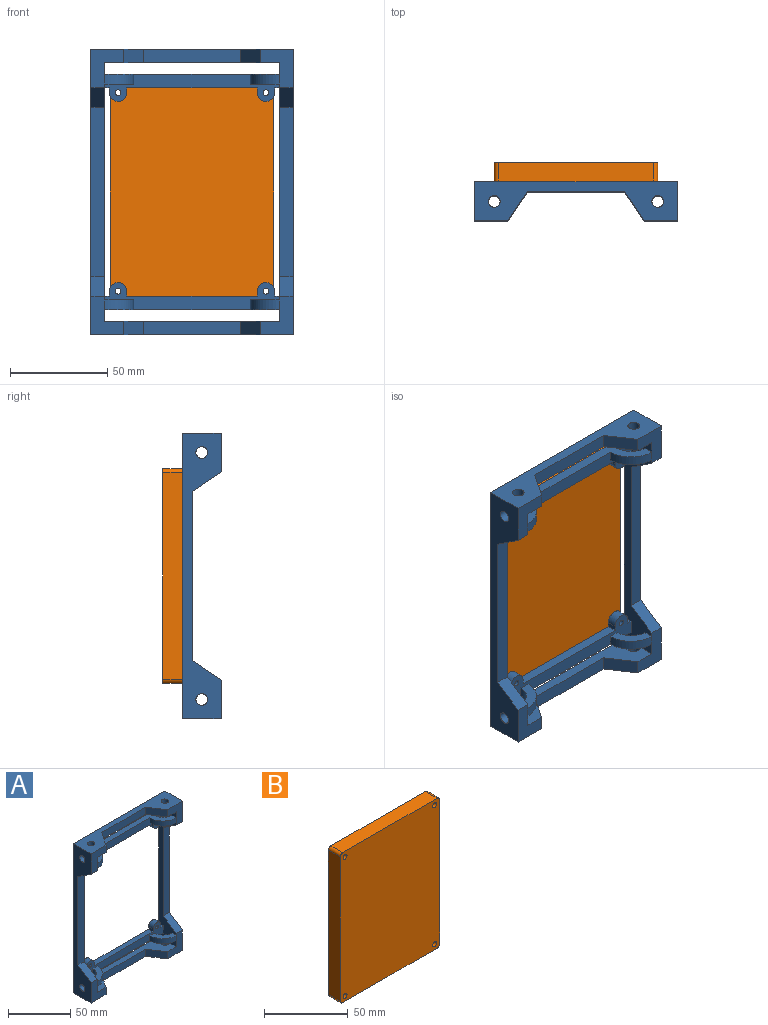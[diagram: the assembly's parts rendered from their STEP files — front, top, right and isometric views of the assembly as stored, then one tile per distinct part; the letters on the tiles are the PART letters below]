
ASSEMBLY  parts=2 mates=1
PART A: 71 faces, bbox 104x20x147 mm
  f0: plane 20x17mm, normal (0,-1,0), area 210mm2, adj f1,f2,f7,f8,f29,f37,f39
  f1: plane 133x20mm, normal (1,0,0), area 1028.5mm2, adj f0,f3,f4,f5,f8,f9,f14,f15
  f2: plane 147x20mm, normal (-1,0,0), area 1428.5mm2, adj f0,f3,f6,f7,f24,f31,f32,f39
  f3: plane 20x17mm, normal (0,-1,0), area 210mm2, adj f1,f2,f6,f21,f25,f33,f40
  f4: plane 90x14mm, normal (0,-1,0), area 674.5mm2, adj f1,f15,f16,f17,f18,f19,f20,f22
  f5: plane 90x14mm, normal (0,-1,0), area 674.5mm2, adj f1,f9,f10,f11,f12,f13,f14,f23
  f6: plane 104x20mm, normal (0,0,1), area 1123.5mm2, adj f2,f3,f24,f33,f34,f35,f44,f45
  f7: plane 104x20mm, normal (0,0,-1), area 1123.5mm2, adj f0,f2,f24,f36,f37,f38,f42,f44
  f8: plane 90x20mm, normal (0,0,1), area 843.5mm2, adj f0,f1,f24,f36,f37,f38,f42,f43
  f9: plane 90x20mm, normal (0,0,-1), area 646.3mm2, adj f1,f5,f24,f28,f29,f43,f59,f60
  f10: plane 67x5mm, normal (0,0,1), area 335mm2, adj f5,f11,f24,f46
  f11: plane 5x2.5mm, normal (1,0,0), area 12.5mm2, adj f5,f10,f12,f24
  f12: cylinder r=4.5mm len=9mm, axis (0,1,0), area 70.7mm2, adj f5,f11,f13,f24
  f13: plane 5x2.5mm, normal (-1,0,0), area 12.5mm2, adj f5,f12,f14,f24
  f14: plane 5x2.5mm, normal (0,0,1), area 12.5mm2, adj f1,f5,f13,f24
  f15: plane 5x2.5mm, normal (0,0,-1), area 12.5mm2, adj f1,f4,f16,f24
  f16: plane 5x2.5mm, normal (-1,0,0), area 12.5mm2, adj f4,f15,f17,f24
  f17: cylinder r=4.5mm len=9mm, axis (0,1,0), area 70.7mm2, adj f4,f16,f18,f24
  f18: plane 5x2.5mm, normal (1,0,0), area 12.5mm2, adj f4,f17,f19,f24
  f19: plane 67x5mm, normal (0,0,-1), area 335mm2, adj f4,f18,f24,f53
  f20: plane 90x20mm, normal (0,0,1), area 646.3mm2, adj f1,f4,f24,f25,f26,f43,f56,f57
  f21: plane 90x20mm, normal (0,0,-1), area 843.5mm2, adj f1,f3,f24,f33,f34,f35,f43,f45
  f22: cylinder r=1.5mm len=5mm, axis (0,1,0), area 47.1mm2, adj f4,f24
  f23: cylinder r=1.5mm len=5mm, axis (0,1,0), area 47.1mm2, adj f5,f24
  f24: plane 147x104mm, normal (0,1,0), area 4767mm2, adj f1,f2,f6,f7,f8,f9,f10,f11
  f25: cylinder r=15mm len=15mm, axis (0,0,1), area 117.8mm2, adj f3,f4,f20,f27
  f26: cylinder r=10mm len=10mm, axis (0,0,1), area 78.5mm2, adj f1,f4,f20,f27
  f27: plane 15x15mm, normal (0,0,-1), area 98.2mm2, adj f1,f4,f25,f26
  f28: cylinder r=10mm len=10mm, axis (0,0,-1), area 78.5mm2, adj f1,f5,f9,f30
  f29: cylinder r=15mm len=15mm, axis (0,0,-1), area 117.8mm2, adj f0,f5,f9,f30
  f30: plane 15x15mm, normal (0,0,1), area 98.2mm2, adj f1,f5,f28,f29
  f31: cylinder r=3mm len=7mm, axis (1,0,0), area 131.9mm2, adj f1,f2
  f32: cylinder r=3mm len=7mm, axis (1,0,0), area 131.9mm2, adj f1,f2
  f33: plane 15x10mm, normal (0.83,-0.55,0), area 126.2mm2, adj f3,f6,f21,f34
  f34: plane 50x7mm, normal (0,-1,0), area 350mm2, adj f6,f21,f33,f64
  f35: cylinder r=3mm len=7mm, axis (0,0,1), area 131.9mm2, adj f6,f21
  f36: plane 50x7mm, normal (0,-1,0), area 350mm2, adj f7,f8,f37,f66
  f37: plane 15x10mm, normal (0.83,-0.55,0), area 126.2mm2, adj f0,f7,f8,f36
  f38: cylinder r=3mm len=7mm, axis (0,0,1), area 131.9mm2, adj f7,f8
  f39: plane 15x10mm, normal (0,-0.55,0.83), area 126.2mm2, adj f0,f1,f2,f41
  f40: plane 15x10mm, normal (0,-0.55,-0.83), area 126.2mm2, adj f1,f2,f3,f41
  f41: plane 87x7mm, normal (0,-1,0), area 609mm2, adj f1,f2,f39,f40
  f42: plane 20x17mm, normal (0,-1,0), area 210mm2, adj f7,f8,f43,f44,f60,f66,f68
  f43: plane 133x20mm, normal (-1,0,0), area 1028.5mm2, adj f4,f5,f8,f9,f20,f21,f24,f42
  f44: plane 147x20mm, normal (1,0,0), area 1428.5mm2, adj f6,f7,f24,f42,f45,f62,f63,f68
  f45: plane 20x17mm, normal (0,-1,0), area 210mm2, adj f6,f21,f43,f44,f56,f64,f69
  f46: plane 5x2.5mm, normal (-1,0,0), area 12.5mm2, adj f5,f10,f24,f47
  f47: cylinder r=4.5mm len=9mm, axis (0,1,0), area 70.7mm2, adj f5,f24,f46,f48
  f48: plane 5x2.5mm, normal (1,0,0), area 12.5mm2, adj f5,f24,f47,f49
  f49: plane 5x2.5mm, normal (0,0,1), area 12.5mm2, adj f5,f24,f43,f48
  f50: plane 5x2.5mm, normal (0,0,-1), area 12.5mm2, adj f4,f24,f43,f51
  f51: plane 5x2.5mm, normal (1,0,0), area 12.5mm2, adj f4,f24,f50,f52
  f52: cylinder r=4.5mm len=9mm, axis (0,1,0), area 70.7mm2, adj f4,f24,f51,f53
  f53: plane 5x2.5mm, normal (-1,0,0), area 12.5mm2, adj f4,f19,f24,f52
  f54: cylinder r=1.5mm len=5mm, axis (0,1,0), area 47.1mm2, adj f4,f24
  f55: cylinder r=1.5mm len=5mm, axis (0,1,0), area 47.1mm2, adj f5,f24
  f56: cylinder r=15mm len=15mm, axis (0,0,1), area 117.8mm2, adj f4,f20,f45,f58
  f57: cylinder r=10mm len=10mm, axis (0,0,1), area 78.5mm2, adj f4,f20,f43,f58
  f58: plane 15x15mm, normal (0,0,-1), area 98.2mm2, adj f4,f43,f56,f57
  f59: cylinder r=10mm len=10mm, axis (0,0,-1), area 78.5mm2, adj f5,f9,f43,f61
  f60: cylinder r=15mm len=15mm, axis (0,0,-1), area 117.8mm2, adj f5,f9,f42,f61
  f61: plane 15x15mm, normal (0,0,1), area 98.2mm2, adj f5,f43,f59,f60
  f62: cylinder r=3mm len=7mm, axis (-1,0,0), area 131.9mm2, adj f43,f44
  f63: cylinder r=3mm len=7mm, axis (-1,0,0), area 131.9mm2, adj f43,f44
  f64: plane 15x10mm, normal (-0.83,-0.55,0), area 126.2mm2, adj f6,f21,f34,f45
  f65: cylinder r=3mm len=7mm, axis (0,0,1), area 131.9mm2, adj f6,f21
  f66: plane 15x10mm, normal (-0.83,-0.55,0), area 126.2mm2, adj f7,f8,f36,f42
  f67: cylinder r=3mm len=7mm, axis (0,0,1), area 131.9mm2, adj f7,f8
  f68: plane 15x10mm, normal (0,-0.55,0.83), area 126.2mm2, adj f42,f43,f44,f70
  f69: plane 15x10mm, normal (0,-0.55,-0.83), area 126.2mm2, adj f43,f44,f45,f70
  f70: plane 87x7mm, normal (0,-1,0), area 609mm2, adj f43,f44,f68,f69
PART B: 14 faces, bbox 84x10x110 mm
  f0: plane 106x10mm, normal (1,0,0), area 1060mm2, adj f8,f9,f10,f13
  f1: plane 80x10mm, normal (0,0,1), area 800mm2, adj f8,f9,f10,f11
  f2: plane 106x10mm, normal (-1,0,0), area 1060mm2, adj f8,f9,f11,f12
  f3: cylinder r=1.7mm len=10mm, axis (0,1,0), area 106.8mm2, adj f8,f9
  f4: cylinder r=1.7mm len=10mm, axis (0,1,0), area 106.8mm2, adj f8,f9
  f5: cylinder r=1.7mm len=10mm, axis (0,1,0), area 106.8mm2, adj f8,f9
  f6: plane 80x10mm, normal (0,0,-1), area 800mm2, adj f8,f9,f12,f13
  f7: cylinder r=1.7mm len=10mm, axis (0,1,0), area 106.8mm2, adj f8,f9
  f8: plane 110x84mm, normal (0,-1,0), area 9200.2mm2, adj f0,f1,f2,f3,f4,f5,f6,f7
  f9: plane 110x84mm, normal (0,1,0), area 9200.2mm2, adj f0,f1,f2,f3,f4,f5,f6,f7
  f10: cylinder r=2mm len=10mm, axis (0,-1,0), area 31.4mm2, adj f0,f1,f8,f9
  f11: cylinder r=2mm len=10mm, axis (0,1,0), area 31.4mm2, adj f1,f2,f8,f9
  f12: cylinder r=2mm len=10mm, axis (0,-1,0), area 31.4mm2, adj f2,f6,f8,f9
  f13: cylinder r=2mm len=10mm, axis (0,1,0), area 31.4mm2, adj f0,f6,f8,f9
PLACE A at identity
PLACE B t=(52,10,0)mm
MATE fastened B.f4 <-> A.f52  axis (0,-1,0) through (90,0,51)mm
